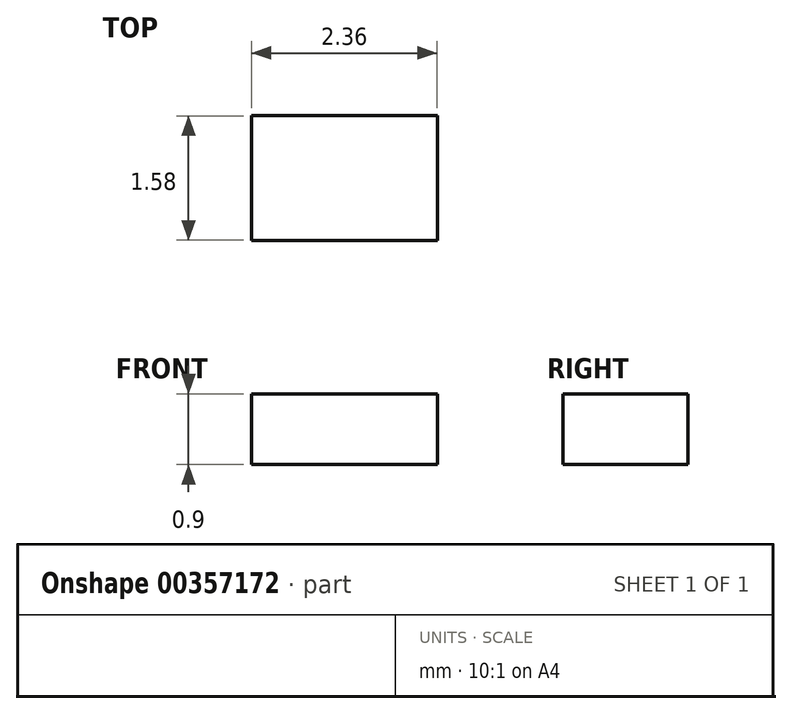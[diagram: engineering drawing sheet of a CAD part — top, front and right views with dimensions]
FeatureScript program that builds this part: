
annotation { "Feature Type Name" : "Feature", "Feature Type Description" : "" }
export const myFeature = defineFeature(function(context is Context, id is Id, definition is map)
    precondition{}
    {
        {
            var Q0;
            Q0=qCreatedBy(makeId("Top.planeOp"),FACE);
            var sketch = newSketch(context, id + "F0", { "sketchPlane" : qUnion([Q0])});
            skLineSegment(sketch, "E0.bottom", {"start": v(1.18, 0.8) * mm, "end": v(-1.18, 0.8) * mm});
            skLineSegment(sketch, "E0.top", {"start": v(1.18, -0.8) * mm, "end": v(-1.18, -0.8) * mm});
            skLineSegment(sketch, "E0.left", {"start": v(1.18, 0.8) * mm, "end": v(1.18, -0.8) * mm});
            skLineSegment(sketch, "E0.right", {"start": v(-1.18, 0.8) * mm, "end": v(-1.18, -0.8) * mm});
            skPoint(sketch, "E0.middle", {"position": v(0, 0) * mm});
            skSolve(sketch);
        }
        {
            var Q0;
            Q0 = qSketchRegion(id + "F0", true);
            extrude(context, id + "F1", {"entities" : qUnion([Q0]), "endBound" : BoundingType.SYMMETRIC, "depth" : 0.9 * mm});
        }
    });
